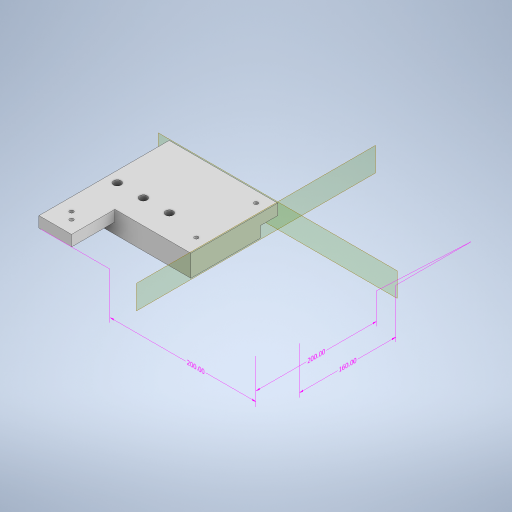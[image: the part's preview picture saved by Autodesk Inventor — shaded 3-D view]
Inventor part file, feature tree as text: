
AUTODESK INVENTOR PART (.ipt)
format: ipt  version: 2023 (Build 270158000, 158)  size: 374,272 bytes
history: native  units: mm
features: sketch x8, other x5, extrude x5, hole x3, plane x2, split x2
ambient origin geometry x8: Origin, YZ Plane, XZ Plane, XY Plane, X Axis, Y Axis, Z Axis, Center Point
bodies: Body1 (feature_tree)
feature tree (25):
  other  "Sólido1"
  other  "Anotaciones"
  extrude  "Extrusión1"  Depth=160.0mm
  extrude  "Extrusión2"  TaperAngle=0.0deg  [1 undecoded]
  extrude  "Extrusión3"  Depth=20.0mm TaperAngle=0.0deg
  extrude  "Extrusión4"  Depth=10.0mm
  hole  "Agujero1"  [1 undecoded]
  plane  "Plano de trabajo1"
  plane  "Plano de trabajo2"
  hole  "Agujero2"  [1 undecoded]
  extrude  "Extrusión5"  Depth=10.0mm
  hole  "Agujero3"  [1 undecoded]
  split  "Dividir1"
  split  "Dividir2"
  sketch  "Boceto1"  dims[d0=200.0mm d1=160.0mm]
  sketch  "Boceto2"  dims[d2=20.0mm d3=0.0mm]
  sketch  "Boceto3"  dims[d4=7.0mm d5=68.0mm d6=80.0mm d7=7.6mm d8=10.0mm d9=7.0mm d10=24.0mm d11=10.0mm d16=0.0mm]
  sketch  "Boceto4"  dims[d19=40.0mm d20=20.0mm d21=0.0mm]
  sketch  "Boceto5"  dims[d22=30.0mm d23=10.0mm]
  sketch  "Boceto6"  dims[d24=40.0mm d25=0.0mm d26=1.75mm]
  sketch  "Boceto7"  dims[d27=8.25mm d28=20.0mm]
  sketch  "Boceto8"  dims[d29=10.0mm d30=10.0mm d31=1.75mm d32=1.75mm d33=1.75mm d34=40.0mm d35=0.0mm d36=11.749873mm d37=40.0mm d38=29.999873mm d39=21.75mm d40=11.75mm d41=28.300341mm d42=11.749873mm d43=0.0mm d44=0.0mm d45=3.5mm d46=6.0mm d47=4.0mm d48=2.0mm d49=90.0deg d50=8.0mm d51=20.594885mm d58=30.0mm d59=30.0mm d63=3.5mm d64=10.0mm d65=10.0mm d66=3.5mm d67=6.0mm d68=4.0mm d69=2.0mm d70=90.0deg d71=8.0mm d72=20.594885mm d73=32.0mm d74=32.0mm d75=10.0mm d76=0.0mm d77=10.0mm d78=30.0mm d79=5.0mm d80=5.0mm d81=5.0mm d82=5.0mm d83=3.5mm d84=6.0mm d85=4.0mm d86=2.0mm d87=90.0deg d88=8.0mm d89=20.594885mm d52=6.692993mm d53=5.009025mm d54=200.0mm d55=6.065637mm d56=3.288093mm d57=200.0mm d60=3.204885mm d61=4.144173mm d62=160.0mm]
  other  "Cota lineal 1"
  other  "Cota lineal 2"
  other  "Cota lineal 3"
note: 4 required parameter values undecoded (feature->parameter linkage not recoverable at this tier; creation-order binding heuristic only, values carry confidence <= 0.55)
